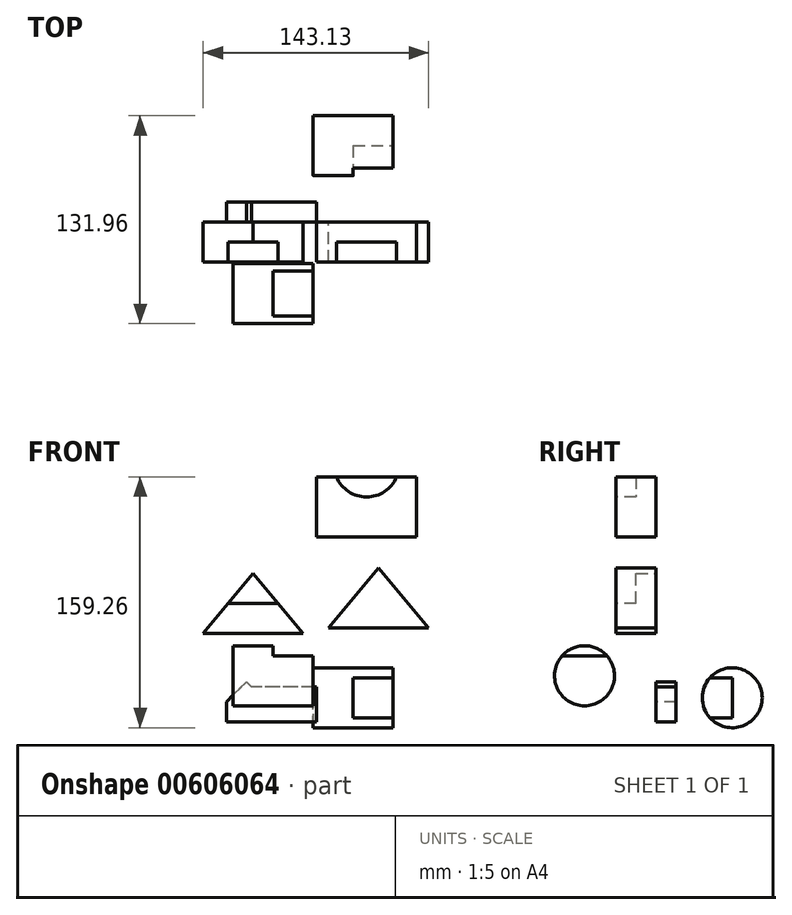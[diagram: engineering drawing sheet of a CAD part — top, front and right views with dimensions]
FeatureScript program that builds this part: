
annotation { "Feature Type Name" : "Feature", "Feature Type Description" : "" }
export const myFeature = defineFeature(function(context is Context, id is Id, definition is map)
    precondition{}
    {
        {
            var Q0;
            Q0=qCreatedBy(makeId("Front.planeOp"),FACE);
            var sketch = newSketch(context, id + "F0", { "sketchPlane" : qUnion([Q0])});
            skLineSegment(sketch, "E0", {"start": v(-69.85, 0.1) * mm, "end": v(-6.35, 0.1) * mm});
            skLineSegment(sketch, "E1", {"start": v(-69.85, 0.1) * mm, "end": v(-38.1, 38.2) * mm});
            skLineSegment(sketch, "E2", {"start": v(-38.1, 38.2) * mm, "end": v(-6.35, 0.1) * mm});
            skSolve(sketch);
        }
        {
            var Q0;
            Q0=makeQuery(id+"F0.imprint","IMPRINT",FACE,{"disambiguationData":[TD([[makeQuery(id+"F0.imprint","IMPRINT",EDGE,{"derivedFrom":sQuery(id+"F0.wireOp",EDGE,"E0")}),1.0]])]});
            extrude(context, id + "F1", {"entities" : qUnion([Q0]), "depth" : 25.4 * mm, "offsetDistance" : 25.4 * mm});
        }
        {
            var Q0;
            Q0=makeQuery(id+"F1.opExtrude","CAP_FACE",FACE,{"disambiguationData":[OSD([sQuery(id+"F0.wireOp",EDGE,"E0"),sQuery(id+"F0.wireOp",EDGE,"E1"),sQuery(id+"F0.wireOp",EDGE,"E2")])],"isStart":false});
            var sketch = newSketch(context, id + "F2", { "sketchPlane" : qUnion([Q0])});
            skLineSegment(sketch, "E3", {"start": v(-38.1, 19.16) * mm, "end": v(-22.22, 19.16) * mm});
            skLineSegment(sketch, "E4", {"start": v(-22.22, 19.16) * mm, "end": v(-38.1, 38.2) * mm});
            skLineSegment(sketch, "E5", {"start": v(-38.1, 38.2) * mm, "end": v(-53.97, 19.16) * mm});
            skLineSegment(sketch, "E6", {"start": v(-53.97, 19.16) * mm, "end": v(-38.1, 19.16) * mm});
            skSolve(sketch);
        }
        {
            var Q0;
            Q0=makeQuery(id+"F2.imprint","IMPRINT",FACE,{"disambiguationData":[TD([[makeQuery(id+"F2.imprint","IMPRINT",EDGE,{"derivedFrom":sQuery(id+"F2.wireOp",EDGE,"E3")}),1.0]])]});
            extrude(context, id + "F3", {"entities" : qUnion([Q0]), "operationType" : NewBodyOperationType.REMOVE, "oppositeDirection" : true, "depth" : 12.7 * mm, "offsetDistance" : 25.4 * mm});
        }
        {
            var Q0;
            Q0=qCreatedBy(makeId("Front.planeOp"),FACE);
            var sketch = newSketch(context, id + "F4", { "sketchPlane" : qUnion([Q0])});
            skLineSegment(sketch, "E7", {"start": v(9.78, 3.68) * mm, "end": v(73.28, 3.68) * mm});
            skLineSegment(sketch, "E8", {"start": v(9.78, 3.68) * mm, "end": v(41.53, 41.78) * mm});
            skLineSegment(sketch, "E9", {"start": v(41.53, 41.78) * mm, "end": v(73.28, 3.68) * mm});
            skLineSegment(sketch, "E10", {"start": v(41.53, 22.73) * mm, "end": v(57.4, 22.73) * mm});
            skLineSegment(sketch, "E11", {"start": v(57.4, 22.73) * mm, "end": v(25.65, 22.73) * mm});
            skSolve(sketch);
        }
        {
            var Q0;
            {var subQ1=sQuery(id+"F4.wireOp",EDGE,"E7");Q0=makeQuery(id+"F4.imprint","IMPRINT",FACE,{"disambiguationData":[TD([[makeQuery(id+"F4.imprint","IMPRINT",EDGE,{"derivedFrom":subQ1}),1.0]])]});}
            var Q1;
            {var subQ3=sQuery(id+"F4.wireOp",EDGE,"E11");var subQ6=makeQuery(id+"F4.imprint","IMPRINT",VERTEX,{"derivedFrom":subQ3});Q1=makeQuery(id+"F4.imprint","IMPRINT",FACE,{"disambiguationData":[TD([[makeQuery(id+"F4.imprint","IMPRINT",EDGE,{"disambiguationData":[TD([[subQ6,1.0]])],"derivedFrom":subQ3}),-1.0]])]});}
            extrude(context, id + "F5", {"entities" : qUnion([Q0, Q1]), "depth" : 25.4 * mm, "offsetDistance" : 25.4 * mm});
        }
        {
            var Q0;
            Q0=qCreatedBy(makeId("Front.planeOp"),FACE);
            var sketch = newSketch(context, id + "F6", { "sketchPlane" : qUnion([Q0])});
            skLineSegment(sketch, "E12", {"start": v(-55.12, -56.11) * mm, "end": v(-29.72, -56.11) * mm});
            skLineSegment(sketch, "E13", {"start": v(-29.72, -56.11) * mm, "end": v(-29.72, -43.41) * mm});
            skLineSegment(sketch, "E14", {"start": v(-55.12, -56.11) * mm, "end": v(-55.12, -43.41) * mm});
            skLineSegment(sketch, "E15", {"start": v(-55.12, -43.41) * mm, "end": v(-42.42, -30.71) * mm});
            skLineSegment(sketch, "E16", {"start": v(-42.42, -30.71) * mm, "end": v(-29.72, -43.41) * mm});
            skLineSegment(sketch, "E17", {"start": v(-29.72, -56.11) * mm, "end": v(2.03, -56.11) * mm});
            skLineSegment(sketch, "E18", {"start": v(2.03, -56.11) * mm, "end": v(2.03, -43.41) * mm});
            skLineSegment(sketch, "E19", {"start": v(2.03, -43.41) * mm, "end": v(-29.72, -43.41) * mm});
            skLineSegment(sketch, "E20", {"start": v(2.03, -43.41) * mm, "end": v(2.03, -33.89) * mm});
            skLineSegment(sketch, "E21", {"start": v(2.03, -33.89) * mm, "end": v(-39.24, -33.89) * mm});
            skSolve(sketch);
        }
        {
            var Q0;
            {var subQ0=sQuery(id+"F6.wireOp",EDGE,"E19");Q0=makeQuery(id+"F6.imprint","IMPRINT",FACE,{"disambiguationData":[TD([[makeQuery(id+"F6.imprint","IMPRINT",EDGE,{"derivedFrom":subQ0}),-1.0]])]});}
            var Q1;
            Q1=makeQuery(id+"F6.imprint","IMPRINT",FACE,{"disambiguationData":[TD([[makeQuery(id+"F6.imprint","IMPRINT",EDGE,{"derivedFrom":sQuery(id+"F6.wireOp",EDGE,"E13")}),-1.0]])]});
            var Q2;
            Q2=makeQuery(id+"F6.imprint","IMPRINT",FACE,{"disambiguationData":[TD([[makeQuery(id+"F6.imprint","IMPRINT",EDGE,{"derivedFrom":sQuery(id+"F6.wireOp",EDGE,"E12")}),1.0]])]});
            extrude(context, id + "F7", {"entities" : qUnion([Q0, Q1, Q2]), "oppositeDirection" : true, "depth" : 12.7 * mm, "offsetDistance" : 25.4 * mm});
        }
        {
            var Q0;
            Q0=qCreatedBy(makeId("Right.planeOp"),FACE);
            var sketch = newSketch(context, id + "F8", { "sketchPlane" : qUnion([Q0])});
            skCircle(sketch, "E22", {"center": v(-45.47, -26.8) * mm, "radius": 19.05 * mm});
            skSolve(sketch);
        }
        {
            var Q0;
            Q0=makeQuery(id+"F8.imprint","IMPRINT",FACE,{"disambiguationData":[TD([[makeQuery(id+"F8.imprint","IMPRINT",EDGE,{"derivedFrom":sQuery(id+"F8.wireOp",EDGE,"E22")}),1.0]])]});
            extrude(context, id + "F9", {"entities" : qUnion([Q0]), "oppositeDirection" : true, "depth" : 50.8 * mm, "offsetDistance" : 25.4 * mm});
        }
        {
            var Q0;
            Q0=makeQuery(id+"F9.opExtrude","CAP_FACE",FACE,{"disambiguationData":[OSD([sQuery(id+"F8.wireOp",EDGE,"E22")])],"isStart":true});
            var sketch = newSketch(context, id + "F10", { "sketchPlane" : qUnion([Q0])});
            skLineSegment(sketch, "E23", {"start": v(-45.47, -14.1) * mm, "end": v(-31.27, -14.1) * mm});
            skLineSegment(sketch, "E24", {"start": v(-45.47, -14.1) * mm, "end": v(-59.67, -14.1) * mm});
            skSolve(sketch);
        }
        {
            var Q0;
            {var subQ0=sQuery(id+"F10.wireOp",EDGE,"E23");Q0=makeQuery(id+"F10.imprint","IMPRINT",FACE,{"disambiguationData":[TD([[makeQuery(id+"F10.imprint","IMPRINT",EDGE,{"derivedFrom":subQ0}),1.0]])]});}
            extrude(context, id + "F11", {"entities" : qUnion([Q0]), "operationType" : NewBodyOperationType.REMOVE, "oppositeDirection" : true, "depth" : 25.4 * mm, "offsetDistance" : 25.4 * mm});
        }
        {
            var Q0;
            Q0=qCreatedBy(makeId("Right.planeOp"),FACE);
            var sketch = newSketch(context, id + "F12", { "sketchPlane" : qUnion([Q0])});
            skCircle(sketch, "E25", {"center": v(48.39, -40.77) * mm, "radius": 19.05 * mm});
            skSolve(sketch);
        }
        {
            var Q0;
            Q0=makeQuery(id+"F12.imprint","IMPRINT",FACE,{"disambiguationData":[TD([[makeQuery(id+"F12.imprint","IMPRINT",EDGE,{"derivedFrom":sQuery(id+"F12.wireOp",EDGE,"E25")}),1.0]])]});
            extrude(context, id + "F13", {"entities" : qUnion([Q0]), "depth" : 50.8 * mm, "offsetDistance" : 25.4 * mm});
        }
        {
            var Q0;
            Q0=makeQuery(id+"F13.opExtrude","CAP_FACE",FACE,{"disambiguationData":[OSD([sQuery(id+"F12.wireOp",EDGE,"E25")])],"isStart":false});
            var sketch = newSketch(context, id + "F14", { "sketchPlane" : qUnion([Q0])});
            skLineSegment(sketch, "E26", {"start": v(48.39, -40.77) * mm, "end": v(48.39, -28.07) * mm});
            skLineSegment(sketch, "E27", {"start": v(48.39, -40.77) * mm, "end": v(48.39, -53.47) * mm});
            skLineSegment(sketch, "E28", {"start": v(48.39, -53.47) * mm, "end": v(34.19, -53.47) * mm});
            skLineSegment(sketch, "E29", {"start": v(48.39, -28.07) * mm, "end": v(34.19, -28.07) * mm});
            skSolve(sketch);
        }
        {
            var Q0;
            Q0=makeQuery(id+"F14.imprint","IMPRINT",FACE,{"disambiguationData":[TD([[makeQuery(id+"F14.imprint","IMPRINT",EDGE,{"derivedFrom":sQuery(id+"F14.wireOp",EDGE,"E26")}),1.0]])]});
            extrude(context, id + "F15", {"entities" : qUnion([Q0]), "operationType" : NewBodyOperationType.REMOVE, "oppositeDirection" : true, "depth" : 25.4 * mm, "offsetDistance" : 25.4 * mm});
        }
        {
            var Q0;
            Q0=qCreatedBy(makeId("Front.planeOp"),FACE);
            var sketch = newSketch(context, id + "F16", { "sketchPlane" : qUnion([Q0])});
            skLineSegment(sketch, "E30", {"start": v(2.16, 61.34) * mm, "end": v(65.66, 61.34) * mm});
            skLineSegment(sketch, "E31", {"start": v(2.16, 61.34) * mm, "end": v(2.16, 99.44) * mm});
            skLineSegment(sketch, "E32", {"start": v(65.66, 61.34) * mm, "end": v(65.66, 99.44) * mm});
            skLineSegment(sketch, "E33", {"start": v(65.66, 99.44) * mm, "end": v(2.16, 99.44) * mm});
            skSolve(sketch);
        }
        {
            var Q0;
            Q0=makeQuery(id+"F16.imprint","IMPRINT",FACE,{"disambiguationData":[TD([[makeQuery(id+"F16.imprint","IMPRINT",EDGE,{"derivedFrom":sQuery(id+"F16.wireOp",EDGE,"E30")}),1.0]])]});
            extrude(context, id + "F17", {"entities" : qUnion([Q0]), "depth" : 25.4 * mm, "offsetDistance" : 25.4 * mm});
        }
        {
            var Q0;
            Q0=makeQuery(id+"F17.opExtrude","CAP_FACE",FACE,{"disambiguationData":[OSD([sQuery(id+"F16.wireOp",EDGE,"E30"),sQuery(id+"F16.wireOp",EDGE,"E31"),sQuery(id+"F16.wireOp",EDGE,"E32"),sQuery(id+"F16.wireOp",EDGE,"E33")])],"isStart":false});
            var sketch = newSketch(context, id + "F18", { "sketchPlane" : qUnion([Q0])});
            skArc(sketch, "E34", {"start": v(14.86, 99.44) * mm, "mid": v(33.9, 86.74) * mm, "end": v(52.96, 99.44) * mm});
            skSolve(sketch);
        }
        {
            var Q0;
            {var subQ0=sQuery(id+"F18.wireOp",EDGE,"E34");Q0=makeQuery(id+"F18.imprint","IMPRINT",FACE,{"disambiguationData":[TD([[makeQuery(id+"F18.imprint","IMPRINT",EDGE,{"derivedFrom":subQ0}),1.0]])]});}
            extrude(context, id + "F19", {"entities" : qUnion([Q0]), "operationType" : NewBodyOperationType.REMOVE, "oppositeDirection" : true, "depth" : 12.7 * mm, "offsetDistance" : 25.4 * mm});
        }
    });
